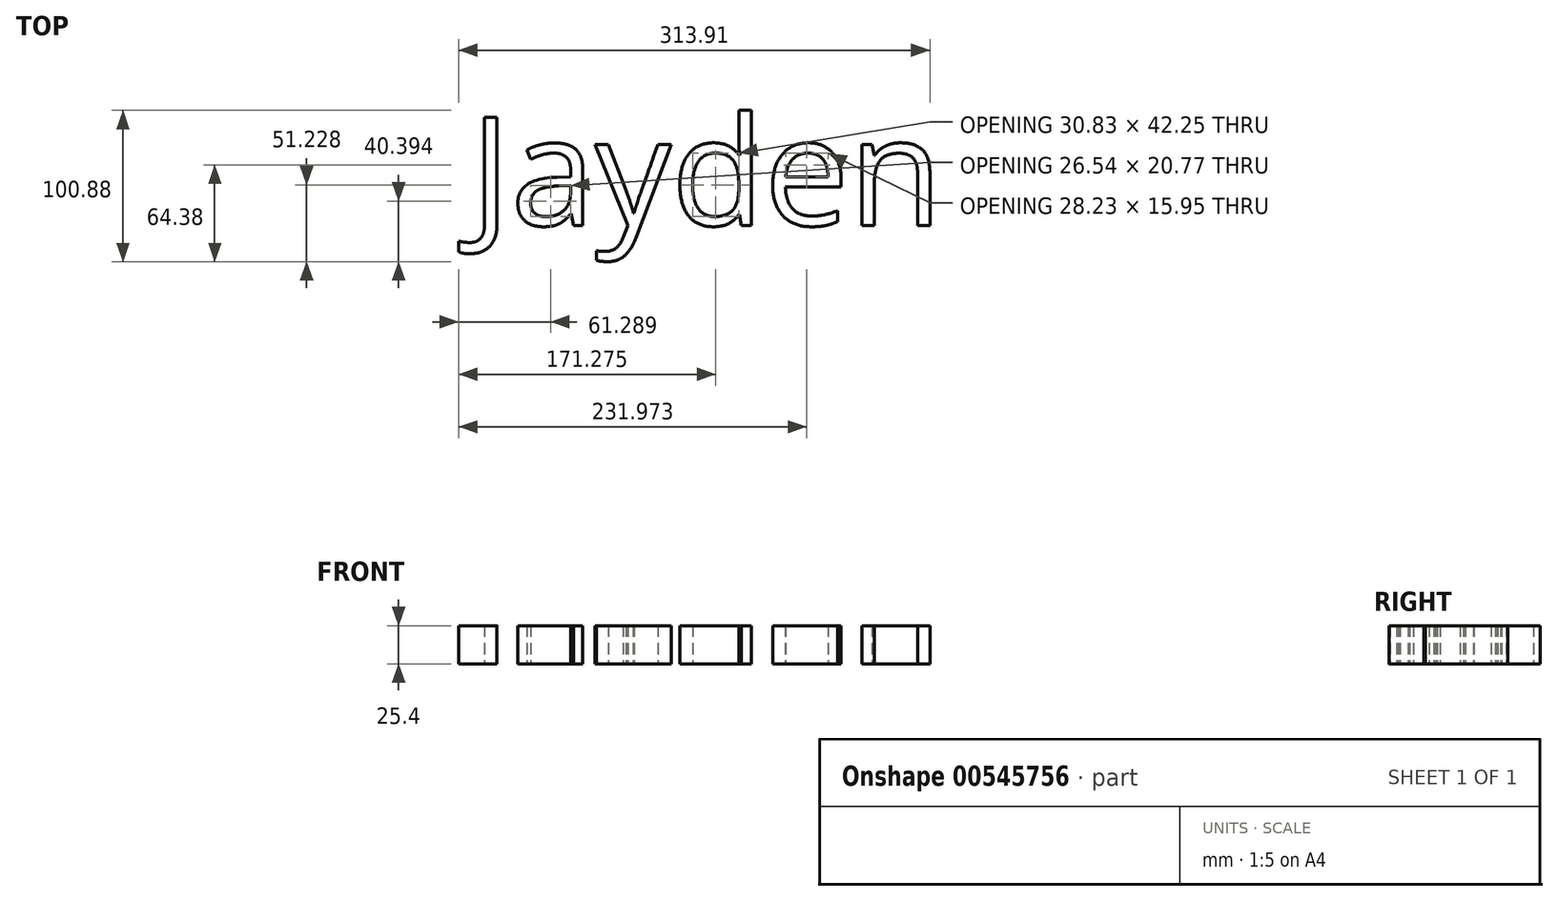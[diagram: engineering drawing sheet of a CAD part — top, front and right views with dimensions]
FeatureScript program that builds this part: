
annotation { "Feature Type Name" : "Feature", "Feature Type Description" : "" }
export const myFeature = defineFeature(function(context is Context, id is Id, definition is map)
    precondition{}
    {
        {
            var Q0;
            Q0=qCreatedBy(makeId("Top.planeOp"),FACE);
            var sketch = newSketch(context, id + "F0", { "sketchPlane" : qUnion([Q0])});
            skText(sketch, "E0", { "text": "Jayden", "fontName": "OpenSans-Regular.ttf"});
            const initialGuessF0  = {"E0": [-0.14815, -0.03361, 1, 0, 0.07262]};
            skSetInitialGuess(sketch, initialGuessF0);
            skSolve(sketch);
        }
        {
            var Q0;
            Q0 = qSketchRegion(id + "F0", true);
            extrude(context, id + "F1", {"entities" : qUnion([Q0]), "depth" : 25.4 * mm, "offsetDistance" : 25.4 * mm});
        }
    });
